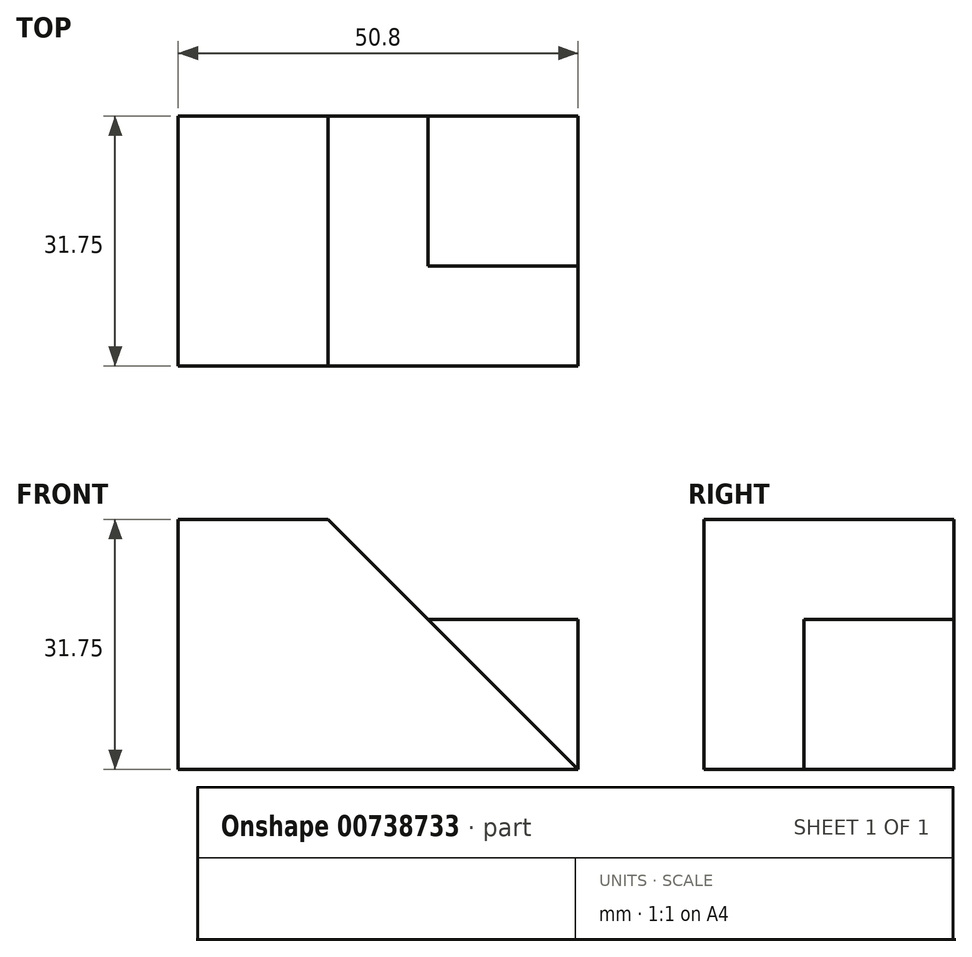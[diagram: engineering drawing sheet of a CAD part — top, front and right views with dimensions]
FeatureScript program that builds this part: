
annotation { "Feature Type Name" : "Feature", "Feature Type Description" : "" }
export const myFeature = defineFeature(function(context is Context, id is Id, definition is map)
    precondition{}
    {
        {
            var Q0;
            Q0=qCreatedBy(makeId("Front.planeOp"),FACE);
            var sketch = newSketch(context, id + "F0", { "sketchPlane" : qUnion([Q0])});
            skLineSegment(sketch, "E0", {"start": v(0, 0) * mm, "end": v(50.8, 0) * mm});
            skLineSegment(sketch, "E1", {"start": v(50.8, 0) * mm, "end": v(50.8, 31.75) * mm});
            skLineSegment(sketch, "E2", {"start": v(50.8, 31.75) * mm, "end": v(0, 31.75) * mm});
            skLineSegment(sketch, "E3", {"start": v(0, 31.75) * mm, "end": v(0, 0) * mm});
            skSolve(sketch);
        }
        {
            var Q0;
            Q0 = qSketchRegion(id + "F0", true);
            extrude(context, id + "F1", {"entities" : qUnion([Q0]), "depth" : 31.75 * mm, "offsetDistance" : 25.4 * mm});
        }
        {
            var Q0;
            Q0=makeQuery(id+"F1.opExtrude","CAP_FACE",FACE,{"disambiguationData":[OSD([sQuery(id+"F0.wireOp",EDGE,"E0"),sQuery(id+"F0.wireOp",EDGE,"E1"),sQuery(id+"F0.wireOp",EDGE,"E2"),sQuery(id+"F0.wireOp",EDGE,"E3")])],"isStart":false});
            var sketch = newSketch(context, id + "F2", { "sketchPlane" : qUnion([Q0])});
            skLineSegment(sketch, "E4", {"start": v(19.05, 31.75) * mm, "end": v(31.75, 19.05) * mm});
            skLineSegment(sketch, "E5", {"start": v(31.75, 19.05) * mm, "end": v(50.8, 19.05) * mm});
            skLineSegment(sketch, "E6", {"start": v(50.8, 19.05) * mm, "end": v(50.8, 31.75) * mm});
            skLineSegment(sketch, "E7", {"start": v(50.8, 31.75) * mm, "end": v(19.05, 31.75) * mm});
            skSolve(sketch);
        }
        {
            var Q0;
            Q0 = qSketchRegion(id + "F2", true);
            extrude(context, id + "F3", {"entities" : qUnion([Q0]), "operationType" : NewBodyOperationType.REMOVE, "oppositeDirection" : true, "depth" : 31.75 * mm, "offsetDistance" : 25.4 * mm});
        }
        {
            var Q0;
            Q0=makeQuery(id+"F1.opExtrude","CAP_FACE",FACE,{"disambiguationData":[OSD([sQuery(id+"F0.wireOp",EDGE,"E0"),sQuery(id+"F0.wireOp",EDGE,"E1"),sQuery(id+"F0.wireOp",EDGE,"E2"),sQuery(id+"F0.wireOp",EDGE,"E3")])],"isStart":false});
            var sketch = newSketch(context, id + "F4", { "sketchPlane" : qUnion([Q0])});
            skLineSegment(sketch, "E8", {"start": v(50.8, 0) * mm, "end": v(50.8, 19.05) * mm});
            skLineSegment(sketch, "E9", {"start": v(50.8, 19.05) * mm, "end": v(31.75, 19.05) * mm});
            skLineSegment(sketch, "E10", {"start": v(31.75, 19.05) * mm, "end": v(50.8, 0) * mm});
            skSolve(sketch);
        }
        {
            var Q0;
            Q0 = qSketchRegion(id + "F4", true);
            extrude(context, id + "F5", {"entities" : qUnion([Q0]), "operationType" : NewBodyOperationType.REMOVE, "oppositeDirection" : true, "depth" : 12.7 * mm, "offsetDistance" : 25.4 * mm});
        }
    });
